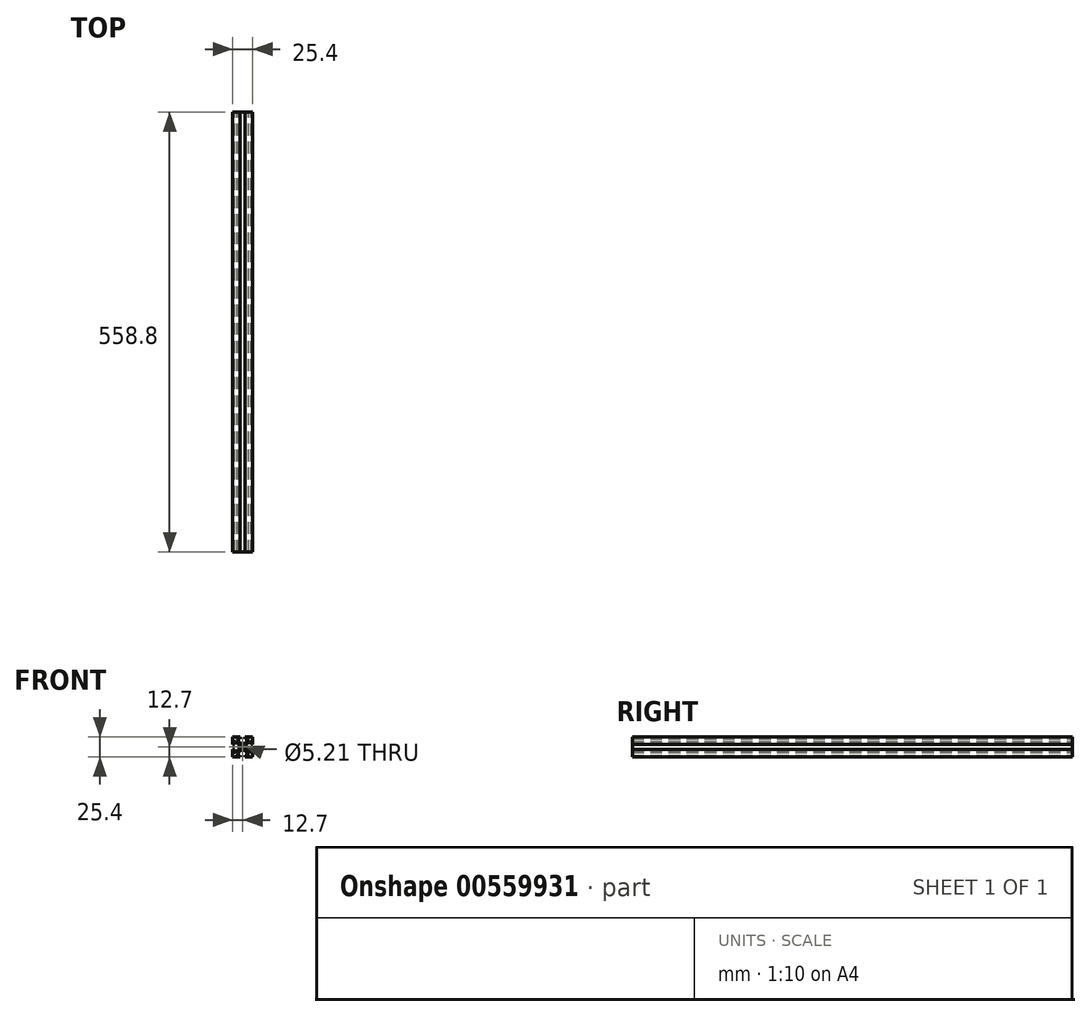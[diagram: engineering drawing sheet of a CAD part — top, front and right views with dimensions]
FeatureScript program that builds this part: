
annotation { "Feature Type Name" : "Feature", "Feature Type Description" : "" }
export const myFeature = defineFeature(function(context is Context, id is Id, definition is map)
    precondition{}
    {
        {
            var Q0;
            Q0=qCreatedBy(makeId("Front.planeOp"),FACE);
            var sketch = newSketch(context, id + "F0", { "sketchPlane" : qUnion([Q0])});
            skCircle(sketch, "E0", {"center": v(0, 0) * mm, "radius": 2.6 * mm});
            skLineSegment(sketch, "E1.bottom", {"start": v(-4.5, 4.5) * mm, "end": v(4.5, 4.5) * mm});
            skLineSegment(sketch, "E1.top", {"start": v(-4.5, -4.5) * mm, "end": v(4.5, -4.5) * mm});
            skLineSegment(sketch, "E1.left", {"start": v(-4.5, 4.5) * mm, "end": v(-4.5, -4.5) * mm});
            skLineSegment(sketch, "E1.right", {"start": v(4.5, 4.5) * mm, "end": v(4.5, -4.5) * mm});
            skLineSegment(sketch, "E2.bottom", {"start": v(-12.7, 12.7) * mm, "end": v(12.7, 12.7) * mm});
            skLineSegment(sketch, "E2.top", {"start": v(-12.7, -12.7) * mm, "end": v(12.7, -12.7) * mm});
            skLineSegment(sketch, "E2.left", {"start": v(-12.7, 12.7) * mm, "end": v(-12.7, -12.7) * mm});
            skLineSegment(sketch, "E2.right", {"start": v(12.7, 12.7) * mm, "end": v(12.7, -12.7) * mm});
            skLineSegment(sketch, "E3.bottom", {"start": v(-3.24, 12.7) * mm, "end": v(3.24, 12.7) * mm});
            skLineSegment(sketch, "E3.top", {"start": v(-3.24, 4.5) * mm, "end": v(3.24, 4.5) * mm});
            skLineSegment(sketch, "E3.left", {"start": v(-3.24, 12.7) * mm, "end": v(-3.24, 10.5) * mm});
            skLineSegment(sketch, "E3.right", {"start": v(3.24, 12.7) * mm, "end": v(3.24, 10.5) * mm});
            skLineSegment(sketch, "E4.bottom", {"start": v(-7.43, 10.5) * mm, "end": v(-3.24, 10.5) * mm});
            skLineSegment(sketch, "E5", {"start": v(-7.43, 10.5) * mm, "end": v(-3.24, 4.5) * mm});
            skLineSegment(sketch, "E6", {"start": v(3.24, 4.5) * mm, "end": v(7.43, 10.5) * mm});
            skLineSegment(sketch, "E7.trimOffspring", {"start": v(3.24, 10.5) * mm, "end": v(7.43, 10.5) * mm});
            skLineSegment(sketch, "E8.bottom", {"start": v(-12.7, 3.24) * mm, "end": v(-10.5, 3.24) * mm});
            skLineSegment(sketch, "E8.top", {"start": v(-12.7, -3.24) * mm, "end": v(-10.5, -3.24) * mm});
            skLineSegment(sketch, "E8.left", {"start": v(-12.7, 3.24) * mm, "end": v(-12.7, -3.24) * mm});
            skLineSegment(sketch, "E8.right", {"start": v(-4.5, 3.24) * mm, "end": v(-4.5, -3.24) * mm});
            skLineSegment(sketch, "E9.left", {"start": v(-10.5, 7.43) * mm, "end": v(-10.5, 3.24) * mm});
            skLineSegment(sketch, "E10", {"start": v(-10.5, 7.43) * mm, "end": v(-4.5, 3.24) * mm});
            skLineSegment(sketch, "E11.trimOffspring", {"start": v(-10.5, -3.24) * mm, "end": v(-10.5, -7.43) * mm});
            skLineSegment(sketch, "E12.MirrorCS", {"start": v(-3.24, -12.7) * mm, "end": v(-3.24, -10.5) * mm});
            skLineSegment(sketch, "E13.MirrorCS", {"start": v(-7.43, -10.5) * mm, "end": v(-3.24, -10.5) * mm});
            skLineSegment(sketch, "E14.MirrorCS", {"start": v(-7.43, -10.5) * mm, "end": v(-3.24, -4.5) * mm});
            skLineSegment(sketch, "E15.MirrorCS", {"start": v(3.24, -4.5) * mm, "end": v(7.43, -10.5) * mm});
            skLineSegment(sketch, "E16.MirrorCS", {"start": v(3.24, -10.5) * mm, "end": v(7.43, -10.5) * mm});
            skLineSegment(sketch, "E17.MirrorCS", {"start": v(3.24, -12.7) * mm, "end": v(3.24, -10.5) * mm});
            skLineSegment(sketch, "E18.MirrorCS", {"start": v(10.5, 7.43) * mm, "end": v(4.5, 3.24) * mm});
            skLineSegment(sketch, "E19.MirrorCS", {"start": v(10.5, -3.24) * mm, "end": v(10.5, -7.43) * mm});
            skLineSegment(sketch, "E20.MirrorCS", {"start": v(12.7, -3.24) * mm, "end": v(10.5, -3.24) * mm});
            skLineSegment(sketch, "E21.MirrorCS", {"start": v(12.7, 3.24) * mm, "end": v(10.5, 3.24) * mm});
            skLineSegment(sketch, "E22.MirrorCS", {"start": v(10.5, 7.43) * mm, "end": v(10.5, 3.24) * mm});
            skLineSegment(sketch, "E23", {"start": v(-10.5, -7.43) * mm, "end": v(-4.5, -3.24) * mm});
            skLineSegment(sketch, "E24", {"start": v(4.5, -3.24) * mm, "end": v(10.5, -7.43) * mm});
            skSolve(sketch);
        }
        {
            var Q0;
            {var subQ1=sQuery(id+"F0.wireOp",EDGE,"E3.left");Q0=makeQuery(id+"F0.imprint","IMPRINT",FACE,{"disambiguationData":[TD([[makeQuery(id+"F0.imprint","IMPRINT",EDGE,{"derivedFrom":subQ1}),-1.0]])]});}
            var Q1;
            {var subQ3=sQuery(id+"F0.wireOp",EDGE,"E3.right");Q1=makeQuery(id+"F0.imprint","IMPRINT",FACE,{"disambiguationData":[TD([[makeQuery(id+"F0.imprint","IMPRINT",EDGE,{"derivedFrom":subQ3}),1.0]])]});}
            var Q2;
            Q2=makeQuery(id+"F0.imprint","IMPRINT",FACE,{"disambiguationData":[TD([[makeQuery(id+"F0.imprint","IMPRINT",EDGE,{"derivedFrom":sQuery(id+"F0.wireOp",EDGE,"E0")}),-1.0]])]});
            var Q3;
            {var subQ0=sQuery(id+"F0.wireOp",EDGE,"E8.top");Q3=makeQuery(id+"F0.imprint","IMPRINT",FACE,{"disambiguationData":[TD([[makeQuery(id+"F0.imprint","IMPRINT",EDGE,{"derivedFrom":subQ0}),-1.0]])]});}
            var Q4;
            {var subQ9=sQuery(id+"F0.wireOp",EDGE,"E15.MirrorCS");Q4=makeQuery(id+"F0.imprint","IMPRINT",FACE,{"disambiguationData":[TD([[makeQuery(id+"F0.imprint","IMPRINT",EDGE,{"derivedFrom":subQ9}),1.0]])]});}
            extrude(context, id + "F1", {"entities" : qUnion([Q0, Q1, Q2, Q3, Q4]), "depth" : 558.8 * mm, "offsetDistance" : 25.4 * mm});
        }
        {
            var Q0;
            Q0=makeQuery(id+"F1.opExtrude","SWEPT_EDGE",EDGE,{"disambiguationData":[OSD([sQuery(id+"F0.wireOp",EDGE,"E4.bottom"),sQuery(id+"F0.wireOp",EDGE,"E5")])]});
            var Q1;
            Q1=makeQuery(id+"F1.opExtrude","SWEPT_EDGE",EDGE,{"disambiguationData":[OSD([sQuery(id+"F0.wireOp",EDGE,"E6"),sQuery(id+"F0.wireOp",EDGE,"E7.trimOffspring")])]});
            var Q2;
            Q2=makeQuery(id+"F1.opExtrude","SWEPT_EDGE",EDGE,{"disambiguationData":[OSD([sQuery(id+"F0.wireOp",EDGE,"E9.left"),sQuery(id+"F0.wireOp",EDGE,"E10")])]});
            var Q3;
            Q3=makeQuery(id+"F1.opExtrude","SWEPT_EDGE",EDGE,{"disambiguationData":[OSD([sQuery(id+"F0.wireOp",EDGE,"E11.trimOffspring"),sQuery(id+"F0.wireOp",EDGE,"E23")])]});
            var Q4;
            Q4=makeQuery(id+"F1.opExtrude","SWEPT_EDGE",EDGE,{"disambiguationData":[OSD([sQuery(id+"F0.wireOp",EDGE,"E13.MirrorCS"),sQuery(id+"F0.wireOp",EDGE,"E14.MirrorCS")])]});
            var Q5;
            Q5=makeQuery(id+"F1.opExtrude","SWEPT_EDGE",EDGE,{"disambiguationData":[OSD([sQuery(id+"F0.wireOp",EDGE,"E15.MirrorCS"),sQuery(id+"F0.wireOp",EDGE,"E16.MirrorCS")])]});
            var Q6;
            Q6=makeQuery(id+"F1.opExtrude","SWEPT_EDGE",EDGE,{"disambiguationData":[OSD([sQuery(id+"F0.wireOp",EDGE,"E19.MirrorCS"),sQuery(id+"F0.wireOp",EDGE,"E24")])]});
            var Q7;
            Q7=makeQuery(id+"F1.opExtrude","SWEPT_EDGE",EDGE,{"disambiguationData":[OSD([sQuery(id+"F0.wireOp",EDGE,"E18.MirrorCS"),sQuery(id+"F0.wireOp",EDGE,"E22.MirrorCS")])]});
            fillet(context, id + "F2", {"entities" : qUnion([Q0, Q1, Q2, Q3, Q4, Q5, Q6, Q7]), "radius" : 0.25 * mm, "tangentPropagation" : true, "allowEdgeOverflow" : false});
        }
    });
